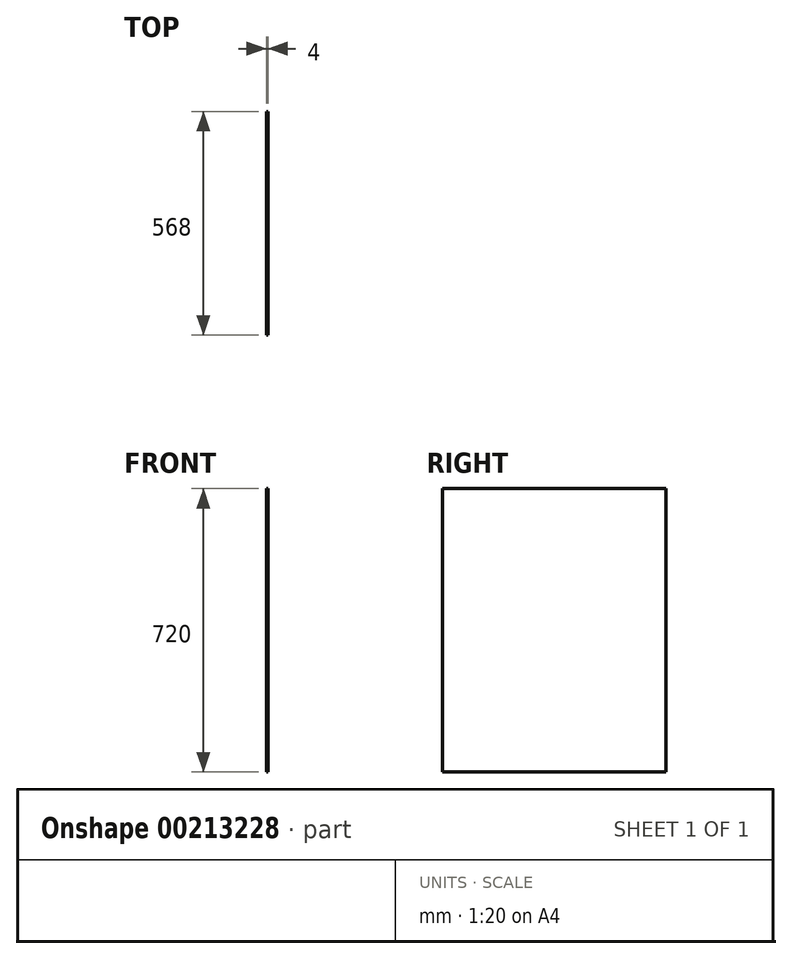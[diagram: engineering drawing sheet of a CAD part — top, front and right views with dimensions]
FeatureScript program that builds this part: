
annotation { "Feature Type Name" : "Feature", "Feature Type Description" : "" }
export const myFeature = defineFeature(function(context is Context, id is Id, definition is map)
    precondition{}
    {
        {
            var Q0;
            Q0=qCreatedBy(makeId("Right.planeOp"),FACE);
            var sketch = newSketch(context, id + "F0", { "sketchPlane" : qUnion([Q0])});
            skLineSegment(sketch, "E0.bottom", {"start": v(284, 360) * mm, "end": v(-284, 360) * mm});
            skLineSegment(sketch, "E0.top", {"start": v(284, -360) * mm, "end": v(-284, -360) * mm});
            skLineSegment(sketch, "E0.left", {"start": v(284, 360) * mm, "end": v(284, -360) * mm});
            skLineSegment(sketch, "E0.right", {"start": v(-284, 360) * mm, "end": v(-284, -360) * mm});
            skPoint(sketch, "E0.middle", {"position": v(0, 0) * mm});
            skSolve(sketch);
        }
        {
            var Q0;
            Q0=makeQuery(id+"F0.imprint","IMPRINT",FACE,{"disambiguationData":[TD([[makeQuery(id+"F0.imprint","IMPRINT",EDGE,{"derivedFrom":sQuery(id+"F0.wireOp",EDGE,"E0.bottom")}),1.0]])]});
            extrude(context, id + "F1", {"entities" : qUnion([Q0]), "endBound" : BoundingType.SYMMETRIC, "depth" : 4 * mm});
        }
    });
